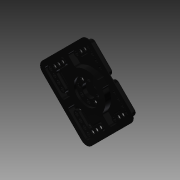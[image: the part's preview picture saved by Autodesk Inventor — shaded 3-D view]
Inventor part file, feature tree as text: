
AUTODESK INVENTOR PART (.ipt)
format: ipt  version: 2015 (Build 190159000, 159)  size: 1,343,488 bytes
history: native  units: mm
features: extrude x9, fillet x7, sketch x5, other x1
ambient origin geometry x8: Origin, YZ Plane, XZ Plane, XY Plane, X Axis, Y Axis, Z Axis, Center Point
bodies: Body1 (feature_tree)
feature tree (22):
  other  "Sólido1"
  sketch  "Boceto1"  dims[d1=40.0mm d2=20.0mm d3=20.0mm d4=5.0mm d5=360.0deg d6=5.0mm d7=5.0mm d8=5.0mm d9=10.0mm d10=2.451216mm d11=270.0mm d12=3.0mm d13=1.0mm d14=0.0mm]
  extrude  "Extrusión1"  Depth=10.0mm TaperAngle=0.0deg
  extrude  "Extrusión2"  Depth=2.0mm
  fillet  "Empalme1"  Radius=36.0mm
  extrude  "Extrusión3"  Depth=2.0mm
  sketch  "Boceto3"  dims[d20=5.0mm d21=2.0mm]
  extrude  "Extrusión4"  Depth=80.0mm TaperAngle=360.0deg
  sketch  "Boceto4"  dims[d22=22.0mm d23=80.0mm d25=360.0deg]
  extrude  "Extrusión5"  Depth=2.0mm
  extrude  "Extrusión6"  Depth=2.0mm
  extrude  "Extrusión7"  Depth=2.0mm
  fillet  "Empalme2"  Radius=5.0mm
  fillet  "Empalme3"  Radius=8.0mm
  sketch  "Boceto5"  dims[d27=2.0mm d28=5.0mm d29=5.0mm d30=5.0mm d31=5.0mm d32=8.0mm d33=8.0mm d34=8.0mm d35=40.0mm d37=360.0deg d39=10.0mm d40=0.0mm d42=40.0mm d43=20.0mm d44=20.0mm d45=5.0mm d46=360.0deg d47=5.0mm d48=5.0mm d49=5.0mm d50=10.0mm d51=2.451216mm d52=270.0mm d53=3.0mm d54=2.0mm d55=2.0mm d56=2.0mm d57=2.0mm d58=8.0mm d59=0.0mm d60=40.0mm d61=2.0mm d62=8.0mm d63=0.0mm d64=2.0mm d65=7.0mm d66=0.0mm d67=5.0mm d68=0.0mm d69=2.0mm d70=1.0mm d71=9.0mm d72=2.0mm d73=5.0mm d74=5.0mm d75=5.0mm d76=5.0mm d77=5.0mm d78=5.0mm d79=5.0mm d80=40.0mm d82=360.0deg d84=7.0mm d85=0.0mm d86=5.0mm d87=0.0mm d88=2.0mm d89=1.0mm d90=1.0mm d91=2.0mm]
  extrude  "Extrusión8"  Depth=2.0mm
  extrude  "Extrusión9"  Depth=2.0mm
  fillet  "Empalme4"  Radius=40.0mm
  fillet  "Empalme5"  Radius=10.0mm
  fillet  "Empalme6"  Radius=2.0mm
  fillet  "Empalme7"  Radius=2.0mm
  sketch  "Boceto2"  dims[d15=10.0mm d16=0.0mm d17=2.0mm d19=36.0mm]
